SOLIDWORKS PART (.sldprt)
format: sldprt  version: not decoded by parser v0  size: 180,224 bytes
history: native  units: mm
features: sketch x4, extrude x2, cut_extrude x2, chamfer x2, material x1 (+13 scaffold rows collapsed)
feature tree (24):
  scaffold x13  (default folders/planes/origin — collapsed)
  material  "Material <not specified>"
  sketch  "Sketch1"  dims[D1=~5.325615mm]
  extrude  "Boss-Extrude1"  Depth=1mm
  sketch  "Sketch2"  dims[D1=0.0mm D2=0.0mm]
  extrude  "Boss-Extrude2"  Depth=8mm
  sketch  "Sketch4"  dims[D1=~6.234317mm]
  cut_extrude  "Cut-Extrude1"  [1 undecoded]
  chamfer  "Chamfer1"  Distance=4mm Angle=45deg
  chamfer  "Chamfer2"  Distance=1mm Angle=45deg
  sketch  "Sketch5"  dims[c1.D1=3.1mm c1.D3=3.1mm c1.D4=3.1mm c1.D2=3.0mm c2.D3=3.0mm]
  cut_extrude  "Cut-Extrude2"  [1 undecoded]
decode coverage: 8 of 10 modeling features carry decoded parameters
note: ~ marks probable driven/reference dimensions
note: 2 parameter values undecoded
note: suppression state not decoded; provenance and decode notes live in map.json
